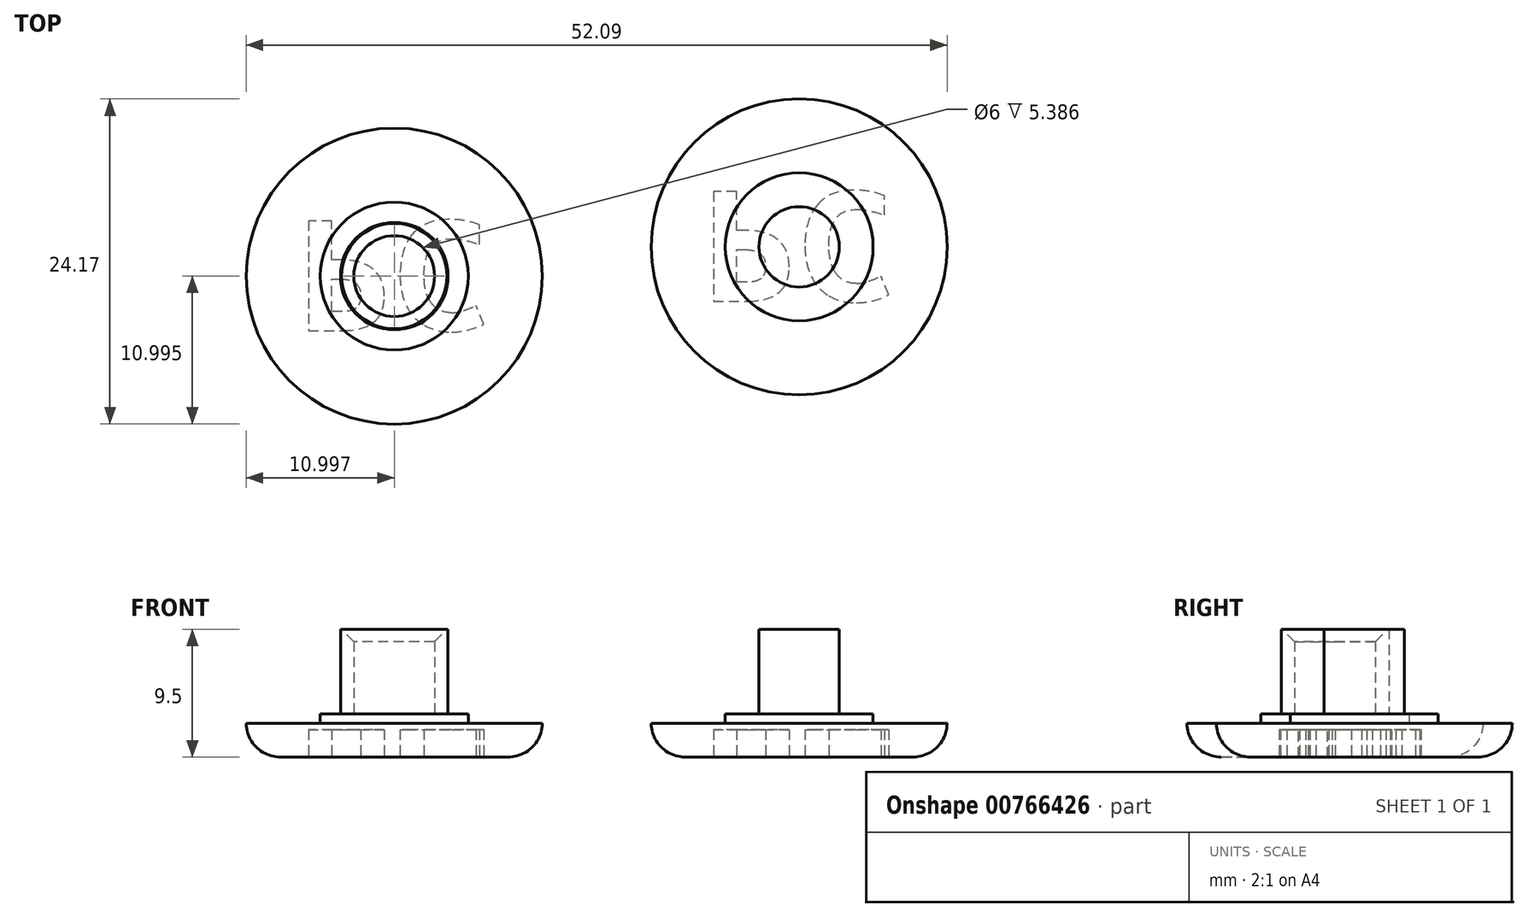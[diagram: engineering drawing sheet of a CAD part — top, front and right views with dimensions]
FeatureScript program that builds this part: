
annotation { "Feature Type Name" : "Feature", "Feature Type Description" : "" }
export const myFeature = defineFeature(function(context is Context, id is Id, definition is map)
    precondition{}
    {
        {
            var Q0;
            Q0=qCreatedBy(makeId("Top.planeOp"),FACE);
            var sketch = newSketch(context, id + "F0", { "sketchPlane" : qUnion([Q0])});
            skCircle(sketch, "E0", {"center": v(8.12, 15.67) * mm, "radius": 11 * mm});
            skCircle(sketch, "E1", {"center": v(-21.97, 13.5) * mm, "radius": 11 * mm});
            skCircle(sketch, "E2", {"center": v(-21.97, 13.5) * mm, "radius": 5.5 * mm});
            skCircle(sketch, "E3", {"center": v(8.12, 15.67) * mm, "radius": 5.5 * mm});
            skSolve(sketch);
        }
        {
            var Q0;
            Q0=makeQuery(id+"F0.imprint","IMPRINT",FACE,{"disambiguationData":[TD([[makeQuery(id+"F0.imprint","IMPRINT",EDGE,{"derivedFrom":sQuery(id+"F0.wireOp",EDGE,"E0")}),1.0]])]});
            var Q1;
            Q1=makeQuery(id+"F0.imprint","IMPRINT",FACE,{"disambiguationData":[TD([[makeQuery(id+"F0.imprint","IMPRINT",EDGE,{"derivedFrom":sQuery(id+"F0.wireOp",EDGE,"E1")}),1.0]])]});
            extrude(context, id + "F1", {"entities" : qUnion([Q0, Q1]), "depth" : 2.5 * mm, "offsetDistance" : 25.4 * mm});
        }
        {
            var Q0;
            Q0=makeQuery(id+"F1.opExtrude","CAP_FACE",FACE,{"disambiguationData":[OSD([sQuery(id+"F0.wireOp",EDGE,"E1")])],"isStart":false});
            var sketch = newSketch(context, id + "F2", { "sketchPlane" : qUnion([Q0])});
            skCircle(sketch, "E4.0.0", {"center": v(-21.97, 13.5) * mm, "radius": 11 * mm});
            skCircle(sketch, "E5", {"center": v(-21.97, 13.5) * mm, "radius": 4 * mm});
            skCircle(sketch, "E6", {"center": v(-21.97, 13.5) * mm, "radius": 3 * mm});
            skSolve(sketch);
        }
        {
            var Q0;
            Q0=makeQuery(id+"F2.imprint","IMPRINT",FACE,{"disambiguationData":[TD([[makeQuery(id+"F2.imprint","IMPRINT",EDGE,{"derivedFrom":sQuery(id+"F2.wireOp",EDGE,"E5")}),1.0]])]});
            extrude(context, id + "F3", {"entities" : qUnion([Q0]), "operationType" : NewBodyOperationType.ADD, "depth" : 7 * mm, "offsetDistance" : 25.4 * mm});
        }
        {
            var Q0;
            Q0=makeQuery(id+"F1.opExtrude","CAP_FACE",FACE,{"disambiguationData":[OSD([sQuery(id+"F0.wireOp",EDGE,"E0")])],"isStart":false});
            var sketch = newSketch(context, id + "F4", { "sketchPlane" : qUnion([Q0])});
            skCircle(sketch, "E7", {"center": v(8.12, 15.67) * mm, "radius": 2.98 * mm});
            skCircle(sketch, "E8.0", {"center": v(-21.97, 13.5) * mm, "radius": 3 * mm});
            skSolve(sketch);
        }
        {
            var Q0;
            Q0=makeQuery(id+"F4.imprint","IMPRINT",FACE,{"disambiguationData":[TD([[makeQuery(id+"F4.imprint","IMPRINT",EDGE,{"derivedFrom":sQuery(id+"F4.wireOp",EDGE,"E7")}),1.0]])]});
            extrude(context, id + "F5", {"entities" : qUnion([Q0]), "operationType" : NewBodyOperationType.ADD, "depth" : 7 * mm, "offsetDistance" : 25.4 * mm});
        }
        {
            var Q0;
            Q0=makeQuery(id+"F1.opExtrude","CAP_EDGE",EDGE,{"disambiguationData":[OSD([sQuery(id+"F0.wireOp",EDGE,"E1")])],"isStart":true});
            var Q1;
            Q1=makeQuery(id+"F1.opExtrude","CAP_EDGE",EDGE,{"disambiguationData":[OSD([sQuery(id+"F0.wireOp",EDGE,"E0")])],"isStart":true});
            fillet(context, id + "F6", {"entities" : qUnion([Q0, Q1]), "radius" : 2.54 * mm, "tangentPropagation" : true, "allowEdgeOverflow" : false});
        }
        {
            var Q0;
            Q0=makeQuery(id+"F0.imprint","IMPRINT",FACE,{"disambiguationData":[TD([[makeQuery(id+"F0.imprint","IMPRINT",EDGE,{"derivedFrom":sQuery(id+"F0.wireOp",EDGE,"E2")}),1.0]])]});
            var Q1;
            Q1=makeQuery(id+"F0.imprint","IMPRINT",FACE,{"disambiguationData":[TD([[makeQuery(id+"F0.imprint","IMPRINT",EDGE,{"derivedFrom":sQuery(id+"F0.wireOp",EDGE,"E3")}),1.0]])]});
            extrude(context, id + "F7", {"entities" : qUnion([Q0, Q1]), "operationType" : NewBodyOperationType.ADD, "depth" : 3.2 * mm, "offsetDistance" : 25.4 * mm});
        }
        {
            var Q0;
            Q0=makeQuery(id+"F3.opExtrude","CAP_EDGE",EDGE,{"disambiguationData":[OSD([sQuery(id+"F2.wireOp",EDGE,"E6")])],"isStart":false});
            chamfer(context, id + "F8", {"entities" : qUnion([Q0]), "width" : 0.91 * mm, "tangentPropagation" : true});
        }
        {
            var Q0;
            {var subQ0=sQuery(id+"F0.wireOp",EDGE,"E2");Q0=makeQuery(id+"F7.boolean.opBoolean","MERGE",FACE,{"derivedFrom":[makeQuery(id+"F1.opExtrude","CAP_FACE",FACE,{"disambiguationData":[OSD([sQuery(id+"F0.wireOp",EDGE,"E1"),subQ0])],"isStart":true}),makeQuery(id+"F7.opExtrude","CAP_FACE",FACE,{"disambiguationData":[OSD([subQ0])],"isStart":true})]});}
            var sketch = newSketch(context, id + "F9", { "sketchPlane" : qUnion([Q0])});
            skText(sketch, "E9", { "text": "PC\n", "fontName": "OpenSans-Bold.ttf"});
            skText(sketch, "E10", { "text": "PC\n", "fontName": "OpenSans-Bold.ttf"});
            const initialGuessF9  = {"E9": [0.00072, -0.01978, 1, 0, 0.00822], "E10": [-0.02937, -0.0176, 1, 0, 0.00822]};
            skSetInitialGuess(sketch, initialGuessF9);
            skSolve(sketch);
        }
        {
            var Q0;
            Q0 = qSketchRegion(id + "F9", true);
            extrude(context, id + "F10", {"entities" : qUnion([Q0]), "operationType" : NewBodyOperationType.REMOVE, "oppositeDirection" : true, "depth" : 2.03 * mm, "offsetDistance" : 25.4 * mm});
        }
    });
